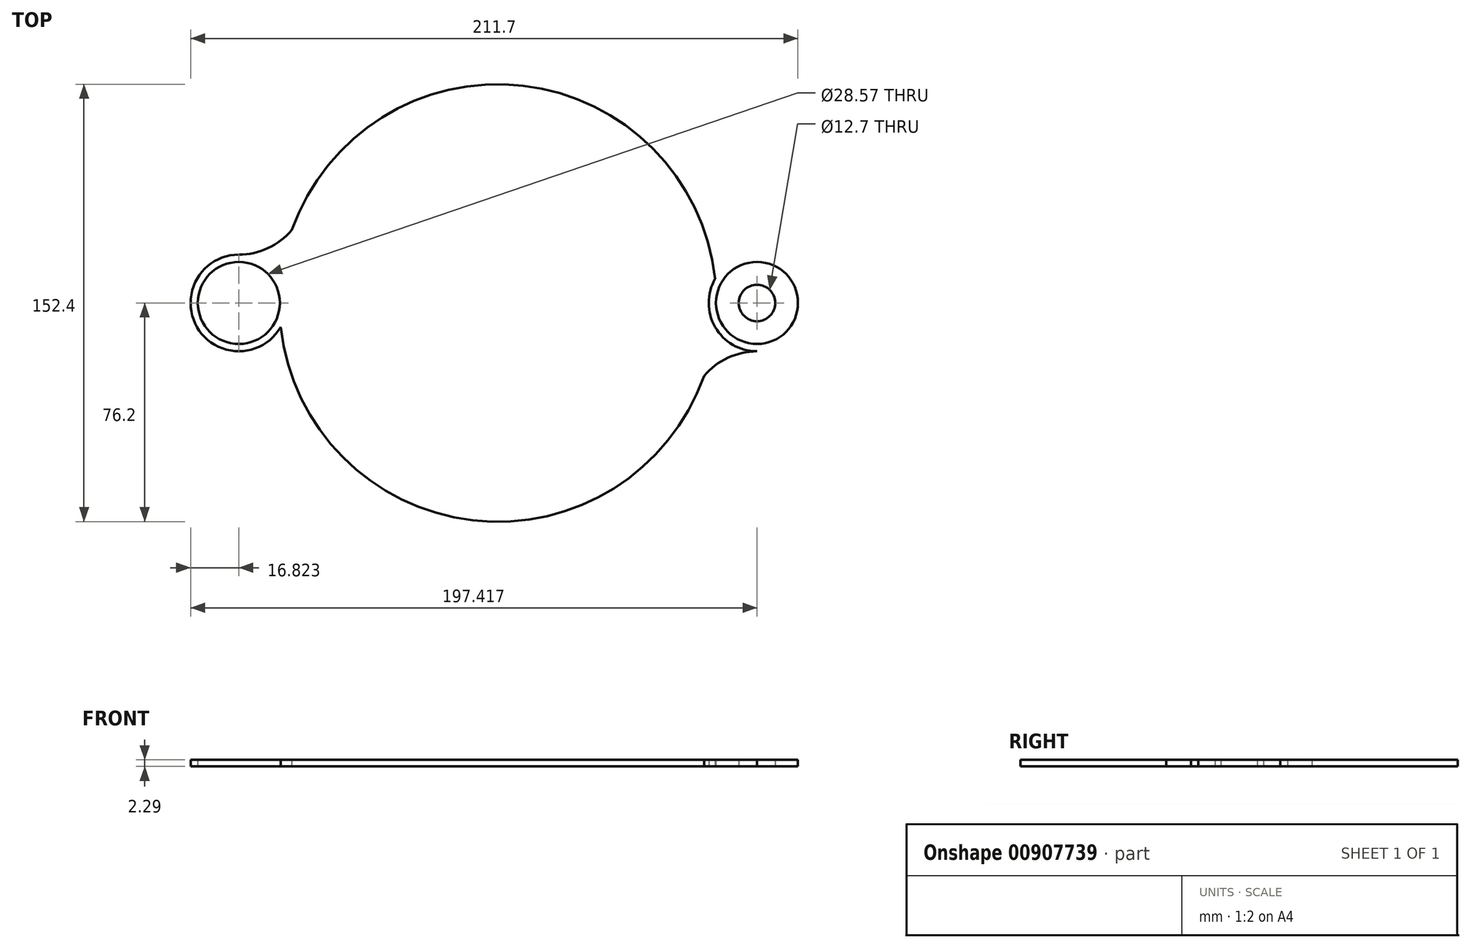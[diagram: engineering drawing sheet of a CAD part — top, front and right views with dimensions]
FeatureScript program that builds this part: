
annotation { "Feature Type Name" : "Feature", "Feature Type Description" : "" }
export const myFeature = defineFeature(function(context is Context, id is Id, definition is map)
    precondition{}
    {
        {
            var Q0;
            Q0=qCreatedBy(makeId("Top.planeOp"),FACE);
            var sketch = newSketch(context, id + "F0", { "sketchPlane" : qUnion([Q0])});
            skArc(sketch, "E0", {"start": v(-61.65, -25.4) * mm, "mid": v(0, -66.68) * mm, "end": v(61.65, -25.4) * mm});
            skArc(sketch, "E1", {"start": v(-71.84, -25.4) * mm, "mid": v(0, -76.2) * mm, "end": v(71.84, -25.4) * mm});
            skPoint(sketch, "E2.orphan", {"position": v(-58.57, -25.4) * mm});
            skPoint(sketch, "E3.orphan", {"position": v(-61.54, 25.4) * mm});
            skArc(sketch, "E4.trimOffspring", {"start": v(61.65, 25.4) * mm, "mid": v(0, 66.68) * mm, "end": v(-61.65, 25.4) * mm});
            skArc(sketch, "E5.trimOffspring", {"start": v(71.84, 25.4) * mm, "mid": v(0, 76.2) * mm, "end": v(-71.84, 25.4) * mm});
            skArc(sketch, "E6", {"start": v(-61.65, -25.4) * mm, "mid": v(-64.1, -18.35) * mm, "end": v(-65.75, -11.06) * mm});
            skArc(sketch, "E7.0", {"start": v(-65.75, 11.06) * mm, "mid": v(-68.95, 16.4) * mm, "end": v(-73.29, 20.87) * mm});
            skArc(sketch, "E8", {"start": v(-71.84, 25.4) * mm, "mid": v(-72.6, 23.15) * mm, "end": v(-73.29, 20.87) * mm});
            skArc(sketch, "E9", {"start": v(-71.84, -25.4) * mm, "mid": v(-72.6, -23.15) * mm, "end": v(-73.29, -20.87) * mm});
            skArc(sketch, "E10.trimOffspring", {"start": v(-65.75, 11.06) * mm, "mid": v(-64.1, 18.35) * mm, "end": v(-61.65, 25.4) * mm});
            skArc(sketch, "E11.trimOffspring", {"start": v(-73.29, -20.87) * mm, "mid": v(-68.95, -16.4) * mm, "end": v(-65.75, -11.06) * mm});
            skArc(sketch, "E12.MirrorCS", {"start": v(73.29, -20.87) * mm, "mid": v(68.95, -16.4) * mm, "end": v(65.75, -11.06) * mm});
            skArc(sketch, "E13.MirrorCS", {"start": v(61.65, -25.4) * mm, "mid": v(64.1, -18.35) * mm, "end": v(65.75, -11.06) * mm});
            skArc(sketch, "E14.MirrorCS", {"start": v(71.84, -25.4) * mm, "mid": v(72.6, -23.15) * mm, "end": v(73.29, -20.87) * mm});
            skArc(sketch, "E15.MirrorCS", {"start": v(65.75, 11.06) * mm, "mid": v(64.1, 18.35) * mm, "end": v(61.65, 25.4) * mm});
            skArc(sketch, "E16.MirrorCS", {"start": v(71.84, 25.4) * mm, "mid": v(72.6, 23.15) * mm, "end": v(73.29, 20.87) * mm});
            skArc(sketch, "E17.MirrorCS", {"start": v(65.75, 11.06) * mm, "mid": v(68.95, 16.4) * mm, "end": v(73.29, 20.87) * mm});
            skCircle(sketch, "E18", {"center": v(-90.3, 0) * mm, "radius": 6.35 * mm});
            skCircle(sketch, "E19", {"center": v(-90.3, 0) * mm, "radius": 14.29 * mm});
            skCircle(sketch, "E20", {"center": v(-90.3, 0) * mm, "radius": 16.83 * mm});
            skArc(sketch, "E21", {"start": v(-73.29, -20.87) * mm, "mid": v(-74.77, -14.7) * mm, "end": v(-75.73, -8.43) * mm});
            skArc(sketch, "E22", {"start": v(-73.29, 20.87) * mm, "mid": v(-74.77, 14.7) * mm, "end": v(-75.73, 8.43) * mm});
            skArc(sketch, "E23", {"start": v(-65.75, 11.06) * mm, "mid": v(-66.68, 0) * mm, "end": v(-65.75, -11.06) * mm});
            skArc(sketch, "E24", {"start": v(-71.84, -25.4) * mm, "mid": v(-80.14, -19.1) * mm, "end": v(-90.3, -16.83) * mm});
            skArc(sketch, "E25.MirrorCS", {"start": v(73.29, -20.87) * mm, "mid": v(74.77, -14.7) * mm, "end": v(75.73, -8.43) * mm});
            skArc(sketch, "E26.MirrorCS", {"start": v(73.29, 20.87) * mm, "mid": v(74.77, 14.7) * mm, "end": v(75.73, 8.43) * mm});
            skCircle(sketch, "E27.MirrorC", {"center": v(90.3, 0) * mm, "radius": 16.83 * mm});
            skCircle(sketch, "E28.MirrorC", {"center": v(90.3, 0) * mm, "radius": 14.29 * mm});
            skCircle(sketch, "E29.MirrorC", {"center": v(90.3, 0) * mm, "radius": 6.35 * mm});
            skArc(sketch, "E30.MirrorCS", {"start": v(71.84, -25.4) * mm, "mid": v(80.14, -19.1) * mm, "end": v(90.3, -16.83) * mm});
            skArc(sketch, "E31.MirrorCS", {"start": v(-71.84, 25.4) * mm, "mid": v(-80.14, 19.1) * mm, "end": v(-90.3, 16.83) * mm});
            skArc(sketch, "E32.MirrorCS", {"start": v(71.84, 25.4) * mm, "mid": v(80.14, 19.1) * mm, "end": v(90.3, 16.83) * mm});
            skSolve(sketch);
        }
        {
            var Q0;
            Q0=makeQuery(id+"F0.imprint","IMPRINT",FACE,{"disambiguationData":[TD([[makeQuery(id+"F0.imprint","IMPRINT",EDGE,{"derivedFrom":sQuery(id+"F0.wireOp",EDGE,"E0")}),1.0]])]});
            var Q1;
            Q1=makeQuery(id+"F0.imprint","IMPRINT",FACE,{"disambiguationData":[TD([[makeQuery(id+"F0.imprint","IMPRINT",EDGE,{"derivedFrom":sQuery(id+"F0.wireOp",EDGE,"E19")}),-1.0]])]});
            var Q2;
            Q2=makeQuery(id+"F0.imprint","IMPRINT",FACE,{"disambiguationData":[TD([[makeQuery(id+"F0.imprint","IMPRINT",EDGE,{"derivedFrom":sQuery(id+"F0.wireOp",EDGE,"E8")}),-1.0]])]});
            var Q3;
            Q3=makeQuery(id+"F0.imprint","IMPRINT",FACE,{"disambiguationData":[TD([[makeQuery(id+"F0.imprint","IMPRINT",EDGE,{"derivedFrom":sQuery(id+"F0.wireOp",EDGE,"E9")}),1.0]])]});
            var Q4;
            Q4=makeQuery(id+"F0.imprint","IMPRINT",FACE,{"disambiguationData":[TD([[makeQuery(id+"F0.imprint","IMPRINT",EDGE,{"derivedFrom":sQuery(id+"F0.wireOp",EDGE,"E7.0")}),1.0]])]});
            var Q5;
            Q5=makeQuery(id+"F0.imprint","IMPRINT",FACE,{"disambiguationData":[TD([[makeQuery(id+"F0.imprint","IMPRINT",EDGE,{"derivedFrom":sQuery(id+"F0.wireOp",EDGE,"E4.trimOffspring")}),-1.0]])]});
            var Q6;
            Q6=makeQuery(id+"F0.imprint","IMPRINT",FACE,{"disambiguationData":[TD([[makeQuery(id+"F0.imprint","IMPRINT",EDGE,{"derivedFrom":sQuery(id+"F0.wireOp",EDGE,"E0")}),-1.0]])]});
            var Q7;
            Q7=makeQuery(id+"F0.imprint","IMPRINT",FACE,{"disambiguationData":[TD([[makeQuery(id+"F0.imprint","IMPRINT",EDGE,{"derivedFrom":sQuery(id+"F0.wireOp",EDGE,"E16.MirrorCS")}),1.0]])]});
            var Q8;
            Q8=makeQuery(id+"F0.imprint","IMPRINT",FACE,{"disambiguationData":[TD([[makeQuery(id+"F0.imprint","IMPRINT",EDGE,{"derivedFrom":sQuery(id+"F0.wireOp",EDGE,"E14.MirrorCS")}),-1.0]])]});
            var Q9;
            Q9=makeQuery(id+"F0.imprint","IMPRINT",FACE,{"disambiguationData":[TD([[makeQuery(id+"F0.imprint","IMPRINT",EDGE,{"derivedFrom":sQuery(id+"F0.wireOp",EDGE,"E28.MirrorC")}),1.0]])]});
            extrude(context, id + "F1", {"entities" : qUnion([Q0, Q1, Q2, Q3, Q4, Q5, Q6, Q7, Q8, Q9]), "depth" : 2.3 * mm, "offsetDistance" : 25.4 * mm});
        }
    });
